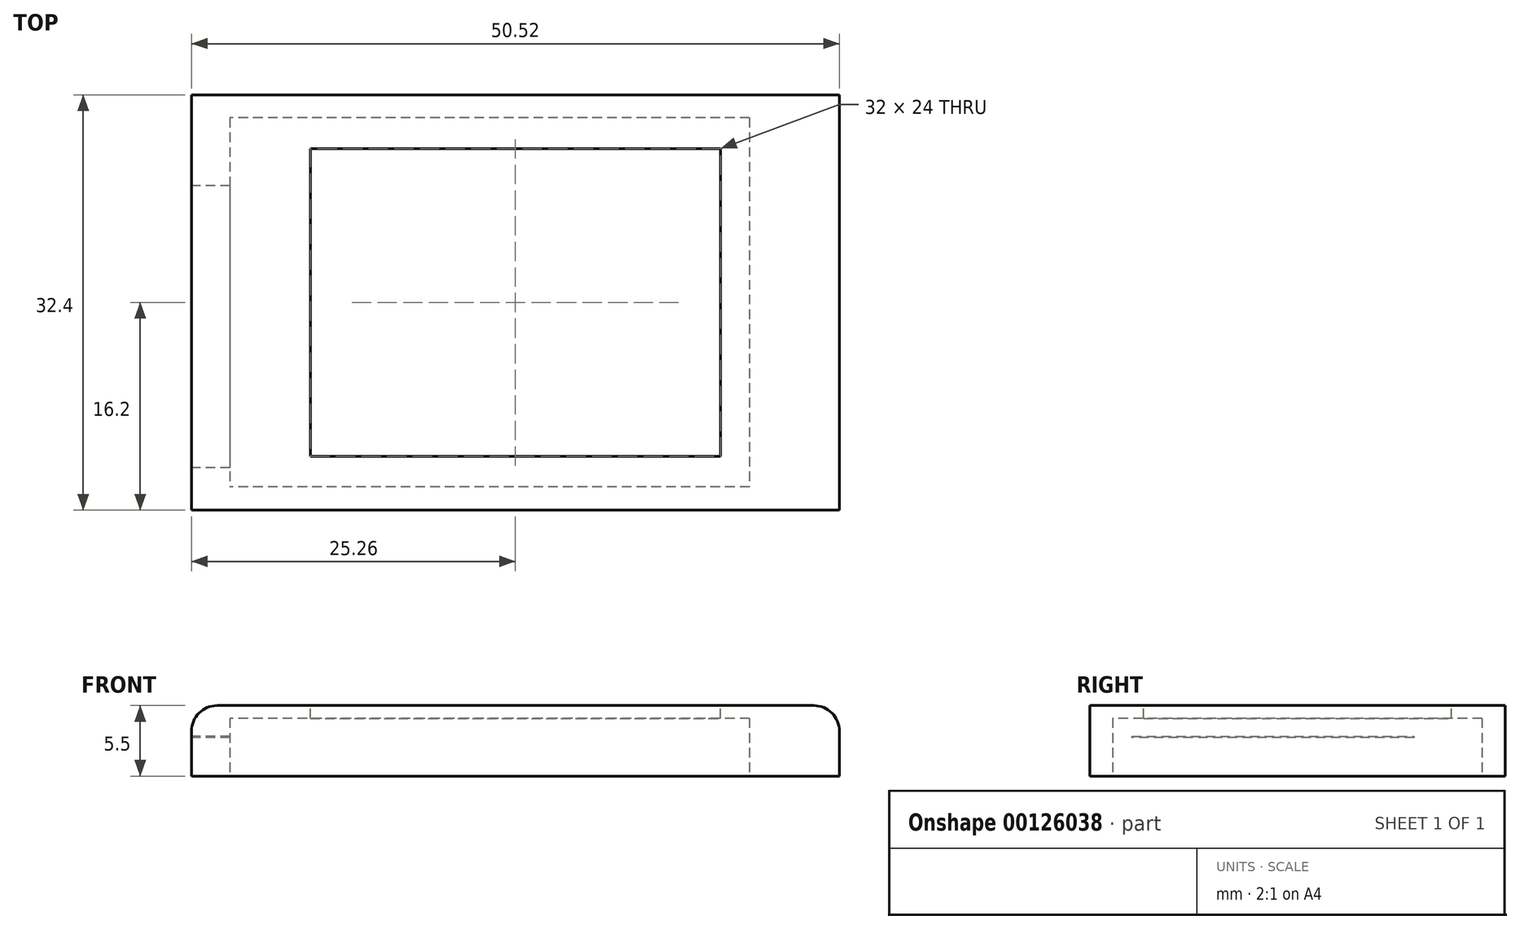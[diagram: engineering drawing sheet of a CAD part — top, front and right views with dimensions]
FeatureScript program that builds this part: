
annotation { "Feature Type Name" : "Feature", "Feature Type Description" : "" }
export const myFeature = defineFeature(function(context is Context, id is Id, definition is map)
    precondition{}
    {
        {
            var Q0;
            Q0=qCreatedBy(makeId("Top.planeOp"),FACE);
            var sketch = newSketch(context, id + "F0", { "sketchPlane" : qUnion([Q0])});
            skLineSegment(sketch, "E0.bottom", {"start": v(18.25, 14.4) * mm, "end": v(-22.26, 14.4) * mm});
            skLineSegment(sketch, "E0.top", {"start": v(18.25, -14.4) * mm, "end": v(-22.26, -14.4) * mm});
            skLineSegment(sketch, "E0.left", {"start": v(18.25, 14.4) * mm, "end": v(18.25, -14.4) * mm});
            skLineSegment(sketch, "E0.right", {"start": v(-22.26, 14.4) * mm, "end": v(-22.26, -14.4) * mm});
            skPoint(sketch, "E0.middle", {"position": v(-2, 0) * mm});
            skLineSegment(sketch, "E1.bottom", {"start": v(14.65, 11) * mm, "end": v(-14.65, 11) * mm});
            skLineSegment(sketch, "E1.top", {"start": v(14.65, -11) * mm, "end": v(-14.65, -11) * mm});
            skLineSegment(sketch, "E1.left", {"start": v(14.65, 11) * mm, "end": v(14.65, -11) * mm});
            skLineSegment(sketch, "E1.right", {"start": v(-14.65, 11) * mm, "end": v(-14.65, -11) * mm});
            skPoint(sketch, "E1.middle", {"position": v(0, 0) * mm});
            skLineSegment(sketch, "E2.bottom", {"start": v(-22.26, -12.9) * mm, "end": v(-25.26, -12.9) * mm});
            skLineSegment(sketch, "E2.top", {"start": v(-22.26, 9.1) * mm, "end": v(-25.26, 9.1) * mm});
            skLineSegment(sketch, "E2.left", {"start": v(-22.26, -12.9) * mm, "end": v(-22.26, 9.1) * mm});
            skLineSegment(sketch, "E2.right", {"start": v(-25.26, -12.9) * mm, "end": v(-25.26, 9.1) * mm});
            skSolve(sketch);
        }
        {
            var Q0;
            {var subQ1=sQuery(id+"F0.wireOp",EDGE,"E0.bottom");Q0=makeQuery(id+"F0.imprint","IMPRINT",FACE,{"disambiguationData":[TD([[makeQuery(id+"F0.imprint","IMPRINT",EDGE,{"derivedFrom":subQ1}),1.0]])]});}
            extrude(context, id + "F1", {"entities" : qUnion([Q0]), "depth" : 1.2 * mm});
        }
        {
            var Q0;
            Q0=makeQuery(id+"F0.imprint","IMPRINT",FACE,{"disambiguationData":[TD([[makeQuery(id+"F0.imprint","IMPRINT",EDGE,{"derivedFrom":sQuery(id+"F0.wireOp",EDGE,"E2.bottom")}),-1.0]])]});
            extrude(context, id + "F2", {"entities" : qUnion([Q0]), "operationType" : NewBodyOperationType.ADD, "depth" : 0.1 * mm});
        }
        {
            var Q0;
            Q0=qCreatedBy(makeId("Front.planeOp"),FACE);
            var sketch = newSketch(context, id + "F3", { "sketchPlane" : qUnion([Q0])});
            skLineSegment(sketch, "E3", {"start": v(-21.97, -1) * mm, "end": v(-17.47, -1) * mm});
            skLineSegment(sketch, "E4", {"start": v(-21.97, -1) * mm, "end": v(-25.26, 0) * mm});
            skSolve(sketch);
        }
        {
            var Q0;
            Q0 = qSketchRegion(id + "F3", true);
            var Q1;
            Q1=sQuery(id+"F3.wireOp",EDGE,"E3");
            var Q2;
            Q2=sQuery(id+"F3.wireOp",EDGE,"E4");
            extrude(context, id + "F4", {"entities" : qUnion([Q0]), "bodyType" : ToolBodyType.SURFACE, "surfaceEntities" : qUnion([Q1, Q2]), "endBound" : BoundingType.SYMMETRIC, "depth" : 10.25 * mm});
        }
        {
            var Q0;
            {var subQ0=sQuery(id+"F0.wireOp",EDGE,"E2.left");Q0=makeQuery(id+"F2.boolean.opBoolean","MERGE",FACE,{"derivedFrom":[makeQuery(id+"F1.opExtrude","CAP_FACE",FACE,{"disambiguationData":[OSD([sQuery(id+"F0.wireOp",EDGE,"E0.bottom"),sQuery(id+"F0.wireOp",EDGE,"E0.top"),sQuery(id+"F0.wireOp",EDGE,"E0.left"),sQuery(id+"F0.wireOp",EDGE,"E0.right"),subQ0])],"isStart":true}),makeQuery(id+"F2.opExtrude","CAP_FACE",FACE,{"disambiguationData":[OSD([sQuery(id+"F0.wireOp",EDGE,"E2.bottom"),sQuery(id+"F0.wireOp",EDGE,"E2.top"),subQ0,sQuery(id+"F0.wireOp",EDGE,"E2.right")])],"isStart":true})]});}
            var sketch = newSketch(context, id + "F5", { "sketchPlane" : qUnion([Q0])});
            skLineSegment(sketch, "E5", {"start": v(-22.26, -14.4) * mm, "end": v(-12.26, -14.4) * mm});
            skLineSegment(sketch, "E6", {"start": v(-12.26, -14.4) * mm, "end": v(-12.26, 10.4) * mm});
            skLineSegment(sketch, "E7", {"start": v(-12.26, 10.4) * mm, "end": v(18.25, 10.4) * mm});
            skLineSegment(sketch, "E8", {"start": v(18.25, 10.4) * mm, "end": v(18.25, 14.4) * mm});
            skLineSegment(sketch, "E9", {"start": v(18.25, 14.4) * mm, "end": v(-22.26, 14.4) * mm});
            skLineSegment(sketch, "E10", {"start": v(-22.26, 14.4) * mm, "end": v(-22.26, -14.4) * mm});
            skSolve(sketch);
        }
        {
            var Q0;
            Q0 = qSketchRegion(id + "F5", true);
            extrude(context, id + "F6", {"entities" : qUnion([Q0]), "depth" : 0.8 * mm});
        }
        {
            var Q0;
            Q0=makeQuery(id+"F0.imprint","IMPRINT",FACE,{"disambiguationData":[TD([[makeQuery(id+"F0.imprint","IMPRINT",EDGE,{"derivedFrom":sQuery(id+"F0.wireOp",EDGE,"E1.bottom")}),1.0]])]});
            extrude(context, id + "F7", {"entities" : qUnion([Q0]), "operationType" : NewBodyOperationType.ADD, "depth" : 1.25 * mm});
        }
        {
            var Q0;
            Q0=qCreatedBy(makeId("Top.planeOp"),FACE);
            var sketch = newSketch(context, id + "F8", { "sketchPlane" : qUnion([Q0])});
            skLineSegment(sketch, "E11.bottom", {"start": v(25.26, -16.2) * mm, "end": v(-25.26, -16.2) * mm});
            skLineSegment(sketch, "E11.top", {"start": v(25.26, 16.2) * mm, "end": v(-25.26, 16.2) * mm});
            skLineSegment(sketch, "E11.left", {"start": v(25.26, -16.2) * mm, "end": v(25.26, 16.2) * mm});
            skLineSegment(sketch, "E11.right", {"start": v(-25.26, -16.2) * mm, "end": v(-25.26, 16.2) * mm});
            skPoint(sketch, "E11.middle", {"position": v(0, 0) * mm});
            skSolve(sketch);
        }
        {
            var Q0;
            Q0 = qSketchRegion(id + "F8", true);
            extrude(context, id + "F9", {"entities" : qUnion([Q0]), "depth" : 2.5 * mm, "hasSecondDirection" : true, "secondDirectionOppositeDirection" : true, "secondDirectionDepth" : 3 * mm});
        }
        {
            var Q0;
            Q0=makeQuery(id+"F9.opExtrude","CAP_FACE",FACE,{"disambiguationData":[OSD([sQuery(id+"F8.wireOp",EDGE,"E11.bottom"),sQuery(id+"F8.wireOp",EDGE,"E11.top"),sQuery(id+"F8.wireOp",EDGE,"E11.left"),sQuery(id+"F8.wireOp",EDGE,"E11.right")])],"isStart":false});
            var sketch = newSketch(context, id + "F10", { "sketchPlane" : qUnion([Q0])});
            skLineSegment(sketch, "E12.bottom", {"start": v(16, 12) * mm, "end": v(-16, 12) * mm});
            skLineSegment(sketch, "E12.top", {"start": v(16, -12) * mm, "end": v(-16, -12) * mm});
            skLineSegment(sketch, "E12.left", {"start": v(16, 12) * mm, "end": v(16, -12) * mm});
            skLineSegment(sketch, "E12.right", {"start": v(-16, 12) * mm, "end": v(-16, -12) * mm});
            skPoint(sketch, "E12.middle", {"position": v(0, 0) * mm});
            skSolve(sketch);
        }
        {
            var Q0;
            Q0 = qSketchRegion(id + "F10", true);
            extrude(context, id + "F11", {"entities" : qUnion([Q0]), "operationType" : NewBodyOperationType.REMOVE, "oppositeDirection" : true, "depth" : 1.2 * mm});
        }
        {
            var Q0;
            Q0 = qSketchRegion(id + "F10", true);
            extrude(context, id + "F12", {"entities" : qUnion([Q0]), "oppositeDirection" : true, "depth" : 1 * mm});
        }
        {
            var Q0;
            {var subQ1=sQuery(id+"F0.wireOp",EDGE,"E0.bottom");Q0=makeQuery(id+"F0.imprint","IMPRINT",FACE,{"disambiguationData":[TD([[makeQuery(id+"F0.imprint","IMPRINT",EDGE,{"derivedFrom":subQ1}),1.0]])]});}
            var Q1;
            Q1=makeQuery(id+"F0.imprint","IMPRINT",FACE,{"disambiguationData":[TD([[makeQuery(id+"F0.imprint","IMPRINT",EDGE,{"derivedFrom":sQuery(id+"F0.wireOp",EDGE,"E1.bottom")}),1.0]])]});
            extrude(context, id + "F13", {"entities" : qUnion([Q0, Q1]), "operationType" : NewBodyOperationType.REMOVE, "depth" : 1.5 * mm, "hasSecondDirection" : true, "secondDirectionOppositeDirection" : true, "secondDirectionDepth" : 3 * mm});
        }
        {
            var Q0;
            Q0=makeQuery(id+"F9.opExtrude","CAP_EDGE",EDGE,{"disambiguationData":[OSD([sQuery(id+"F8.wireOp",EDGE,"E11.right")])],"isStart":false});
            var Q1;
            Q1=makeQuery(id+"F9.opExtrude","CAP_EDGE",EDGE,{"disambiguationData":[OSD([sQuery(id+"F8.wireOp",EDGE,"E11.left")])],"isStart":false});
            fillet(context, id + "F14", {"entities" : qUnion([Q0, Q1]), "radius" : 2 * mm, "tangentPropagation" : true, "allowEdgeOverflow" : false});
        }
    });
